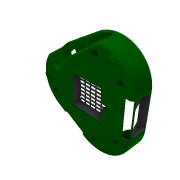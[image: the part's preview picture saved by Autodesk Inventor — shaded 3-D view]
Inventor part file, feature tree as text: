
AUTODESK INVENTOR PART (.ipt)
format: ipt  version: 2016 (Build 200138000, 138)  size: 4,703,744 bytes
history: native  units: in
note: dims shown in document units (in); Inventor stores cm internally (conversion verified against a paired STEP export)
features: projected_geometry x28, sketch x20, extrude x20, fillet x6, plane x2, reference x2, other x1, chamfer x1, pattern_linear x1, boolean_combine x1, imported_body x1
ambient origin geometry x8: Origin, YZ Plane, XZ Plane, XY Plane, X Axis, Y Axis, Z Axis, Center Point
bodies: Solid1 (feature_tree), Solid2 (feature_tree), Solid3 (feature_tree)
feature tree (83):
  other  "bottom_cover-2016-04-29-21"
  sketch  "Sketch1"  dims[d0=0.0709in d1=0.0709in d2=0.3543in]
  plane  "Work Plane1"
  extrude  "Extrusion1"  Depth=0.0709in
  fillet  "Fillet1"  Radius=0.3543in
  extrude  "Extrusion2"  Depth=1.9685in
  extrude  "Extrusion3"  Depth=1.5748in
  plane  "Work Plane2"
  extrude  "Extrusion4"  Depth=2.5591in TaperAngle=0.0deg
  extrude  "Extrusion5"  Depth=0.7902in
  chamfer  "Chamfer1"  Distance=11.811in
  extrude  "Extrusion6"  Depth=0.0787in
  extrude  "Extrusion7"  Depth=4.9213in TaperAngle=0.0deg
  extrude  "Extrusion8"  Depth=0.0866in TaperAngle=45.0deg
  extrude  "Extrusion9"  Depth=7.874in TaperAngle=0.0deg
  extrude  "Extrusion10"  Depth=4.7244in
  extrude  "Extrusion11"  Depth=0.9843in TaperAngle=0.0deg
  pattern_linear  "Rectangular Pattern1"  Count1=2 Spacing1=0.0in
  boolean_combine  "Combine1"
  extrude  "Extrusion12"  Depth=3.1496in
  extrude  "Extrusion13"  Depth=1.1811in
  extrude  "Extrusion14"  Depth=1.1811in TaperAngle=0.0deg
  extrude  "Extrusion15"  Depth=1.1811in TaperAngle=0.0deg
  fillet  "Fillet2"  Radius=0.0787in
  extrude  "Extrusion16"  Depth=0.1181in
  fillet  "Fillet3"  Radius=1.1811in
  extrude  "Extrusion17"  Depth=0.0394in TaperAngle=0.0deg
  extrude  "Extrusion18"  Depth=2.7165in
  extrude  "Extrusion19"  Depth=2.7165in
  fillet  "Fillet5"  Radius=1.5748in
  fillet  "Fillet6"  Radius=2.7165in
  fillet  "Fillet7"  Radius=0.1181in
  extrude  "Extrusion20"  [1 undecoded]
  imported_body  "Base1"
  reference  "Reference1"
  reference  "Reference2"
  sketch  "Sketch5"  dims[d3=0.3543in d4=1.9685in]
  projected_geometry  "Projected Loop1"
  sketch  "Sketch6"  dims[d5=1.5748in d6=0.3937in d7=-0.0069in]
  projected_geometry  "Projected Loop2"
  sketch  "Sketch7"  dims[d8=0.1969in d9=2.5591in d10=0.0in]
  projected_geometry  "Projected Loop3"
  sketch  "Sketch8"  dims[d11=45.0deg d12=0.7902in d13=11.811in d14=0.0in]
  projected_geometry  "Projected Loop4"
  sketch  "Sketch9"  dims[d15=-0.1181in d16=0.0787in]
  projected_geometry  "Projected Loop5"
  sketch  "Sketch10"  dims[d17=0.0787in d18=4.9213in d19=0.0in]
  projected_geometry  "Projected Loop6"
  sketch  "Sketch11"  dims[d20=0.1969in d21=0.0in d22=0.0866in d23=0.0787in d24=45.0deg]
  projected_geometry  "Projected Loop7"
  sketch  "Sketch12"  dims[d25=7.874in d26=0.0in d27=7.874in d28=0.0in]
  projected_geometry  "Projected Loop8"
  sketch  "Sketch13"  dims[d29=0.2362in d30=0.0in d31=4.7244in]
  projected_geometry  "Projected Loop9"
  projected_geometry  "Projected Loop10"
  sketch  "Sketch14"  dims[d32=4.7244in d33=0.9843in d34=0.0in]
  projected_geometry  "Projected Loop11"
  sketch  "Sketch15"  dims[d35=0.1181in]
  projected_geometry  "Projected Loop12"
  sketch  "Sketch16"  dims[d36=0.9843in d37=0.0in d38=0.7874in d39=0.0in]
  projected_geometry  "Projected Loop13"
  projected_geometry  "Projected Loop14"
  projected_geometry  "Projected Loop15"
  projected_geometry  "Projected Loop16"
  sketch  "Sketch17"  dims[d40=1.9685in d42=0.8661in d43=3.1496in d45=0.5512in]
  projected_geometry  "Projected Loop17"
  sketch  "Sketch18"  dims[d46=0.1181in d47=0.0in d48=1.1811in d49=0.0137in]
  projected_geometry  "Projected Loop18"
  projected_geometry  "Projected Loop19"
  sketch  "Sketch19"  dims[d50=0.9843in d51=1.1811in d52=0.0in]
  projected_geometry  "Projected Loop20"
  sketch  "Sketch20"  dims[d53=0.1181in d54=1.1811in d55=0.0in d56=0.0787in]
  projected_geometry  "Projected Loop21"
  sketch  "Sketch21"  dims[d57=1.1811in d58=0.0in d59=0.1181in d61=1.1811in d62=0.0in]
  projected_geometry  "Projected Loop22"
  sketch  "Sketch22"  dims[d63=1.1811in d64=0.0in d65=0.0394in d66=0.0in]
  projected_geometry  "Projected Loop23"
  projected_geometry  "Projected Loop24"
  projected_geometry  "Projected Loop25"
  sketch  "Sketch24"  dims[d67=0.1969in d68=0.1575in d69=0.0472in d70=1.5748in d71=2.7165in d72=0.1181in d73=0.0in]
  projected_geometry  "Projected Loop27"
  projected_geometry  "Project Cut Edges1"
  projected_geometry  "Project Cut Edges2"
note: 1 required parameter value undecoded (feature->parameter linkage not recoverable at this tier; creation-order binding heuristic only, values carry confidence <= 0.55)
